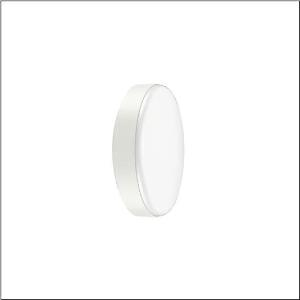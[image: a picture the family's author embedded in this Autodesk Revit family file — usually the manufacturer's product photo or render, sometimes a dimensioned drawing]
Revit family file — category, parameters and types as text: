
# Revit family: rondel_31_51wc10da42a
name_source: partatom
category: Lighting Fixtures
units: mm (PartAtom-declared; Revit-internal decimal feet)

## family parameters
Cut with Voids When Loaded = No
Host = Face
Light Source = No
Part Type = Normal
Room Calculation Point = No
Round Connector Dimension = Use Diameter
Shared = No

## types (1)
- Rondel 31 (1 x LED, 2550 lm, 19 W, 4000K)
    Apparent Load = 19 VA
    CIE Flux Codes = 44 75 94 94 100
    Color Rendering = 80
    Color Temperature = 4000K
    Default Elevation = 1800 mm
    Description = Rondel 31, wall and ceiling luminaire, primary optical cover: cover, of PC, opal, light emission: direct distribution, primary light characteristic: symmetric, installation type: surface-mounted, LED, rated luminous flux: 2.550lm, luminous efficacy: 134lm/W, light colour: 840, colour temperature: 4000K, with terminal, 5-pole, max. 2.5mm², mains connection: 220..240V, AC, 50/60Hz, rated input power: 19W, luminaire housing, of PC, traffic white (RAL 9016), diameter: 350mm, protection rating (complete): IP65, insulation class (complete): insulation class II (safety insulation), certification: CE, impact resistance: IK10, permissible operating ambient temperature: -20..+40°C, permissible storage temperature: -20..+60°C, packaging unit: 1 piece
    Height = 97 mm
    Lamp = 1 x LED
    Lamp Light Flux = 2550 lm
    Lamp Power = 19 W
    Lamp count = 1
    Length = 350 mm
    Luminous efficacy = 134 lm/W
    Manufacturer = Siteco
    ModVariant = No
    Model = 51WC10DA42A
    Mounting Place = Ceiling
    Mounting Type = Surface mounted
    Number of Poles = 1
    OnlyDefault = Yes
    Power Factor = 1
    Product Name = Rondel 31
    Product group = wall and ceiling luminaire
    ProductGroupID = 302
    Protection Class = Protection class II
    Protection Degree = IP 65
    RLX_Detail_Level = 1
    RLX_Emergency_Light_Flux = 0 lm
    RLX_Emergency_Type = 0
    RLX_Emergency_Type_DB = No
    RlxData = <blob elided: 29601 chars, md5=f6ad6ed6>
    Socket = socket
    Standby Power = 0 W
    System Light Flux = 2550 lm
    System Power = 19 W
    Type Comments = Product without accessories
    Type Image = l_1007027.jpg
    URL = http://relux.com
    VarID = ---
    Voltage = 0 V
    Weight = 0.00 kg
    Width = 0 mm  [stored 0 ft]

note: [stored X ft] marks values corroborated as IEEE doubles in the binary element streams (Revit-internal decimal feet)

## geometry (parser evidence)
native form markers: Blend x4, Sweep x10
no freeform markers — native parametric forms only
